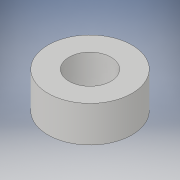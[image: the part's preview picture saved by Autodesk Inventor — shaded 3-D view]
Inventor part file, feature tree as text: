
AUTODESK INVENTOR PART (.ipt)
format: ipt  version: 2017 (Build 210142000, 142)  size: 94,720 bytes
history: native  units: in
note: dims shown in document units (in); Inventor stores cm internally (conversion verified against a paired STEP export)
features: extrude x1, sketch x1
ambient origin geometry x8: Origin, YZ Plane, XZ Plane, XY Plane, X Axis, Y Axis, Z Axis, Center Point
bodies: Solid1 (feature_tree)
feature tree (2):
  extrude  "Extrusion1"  Depth=0.215in
  sketch  "Sketch1"  dims[d0=0.25in d1=0.5in d2=0.215in d3=0.0in]
